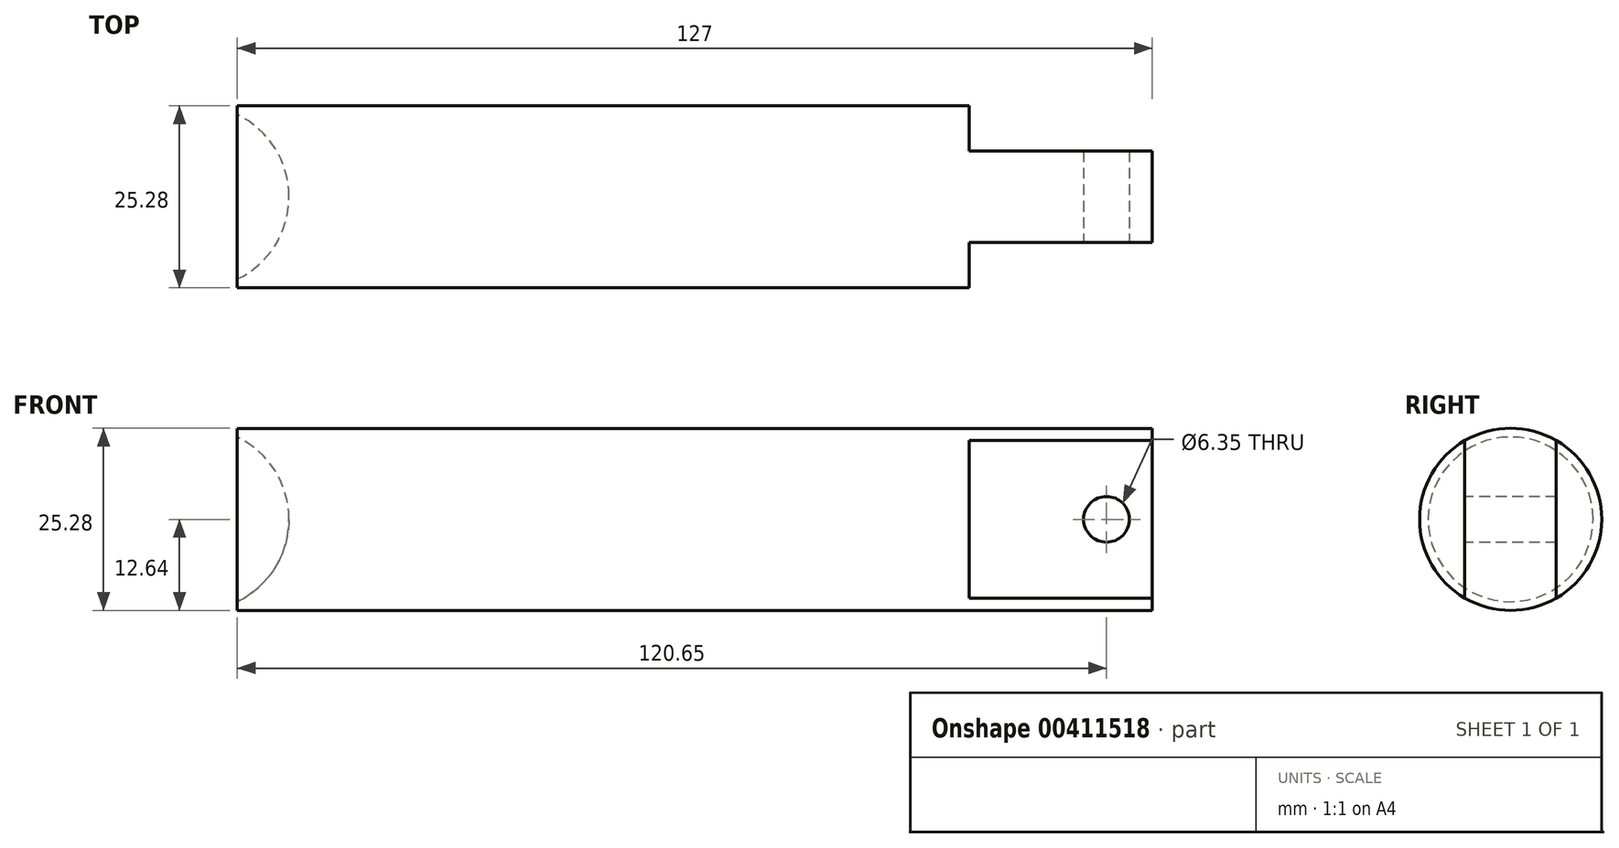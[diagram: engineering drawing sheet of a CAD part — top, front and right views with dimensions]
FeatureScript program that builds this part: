
annotation { "Feature Type Name" : "Feature", "Feature Type Description" : "" }
export const myFeature = defineFeature(function(context is Context, id is Id, definition is map)
    precondition{}
    {
        {
            var Q0;
            Q0=qCreatedBy(makeId("Right.planeOp"),FACE);
            var sketch = newSketch(context, id + "F0", { "sketchPlane" : qUnion([Q0])});
            skCircle(sketch, "E0", {"center": v(0, 0) * mm, "radius": 12.64 * mm});
            skSolve(sketch);
        }
        {
            var Q0;
            Q0 = qSketchRegion(id + "F0", true);
            extrude(context, id + "F1", {"entities" : qUnion([Q0]), "depth" : 127 * mm});
        }
        {
            var Q0;
            Q0=makeQuery(id+"F1.opExtrude","CAP_FACE",FACE,{"disambiguationData":[OSD([sQuery(id+"F0.wireOp",EDGE,"E0")])],"isStart":false});
            var sketch = newSketch(context, id + "F2", { "sketchPlane" : qUnion([Q0])});
            skArc(sketch, "E1.0", {"start": v(6.35, -10.93) * mm, "mid": v(12.64, 0) * mm, "end": v(6.35, 10.93) * mm});
            skLineSegment(sketch, "E2", {"start": v(-6.35, 10.93) * mm, "end": v(-6.35, -10.93) * mm});
            skLineSegment(sketch, "E3", {"start": v(6.35, 10.93) * mm, "end": v(6.35, -10.93) * mm});
            skArc(sketch, "E4.trimOffspring", {"start": v(-6.35, 10.93) * mm, "mid": v(-12.64, 0) * mm, "end": v(-6.35, -10.93) * mm});
            skSolve(sketch);
        }
        {
            var Q0;
            Q0=makeQuery(id+"F2.imprint","IMPRINT",FACE,{"disambiguationData":[TD([[makeQuery(id+"F2.imprint","IMPRINT",EDGE,{"derivedFrom":sQuery(id+"F2.wireOp",EDGE,"E2")}),-1.0]])]});
            var Q1;
            Q1=makeQuery(id+"F2.imprint","IMPRINT",FACE,{"disambiguationData":[TD([[makeQuery(id+"F2.imprint","IMPRINT",EDGE,{"derivedFrom":sQuery(id+"F2.wireOp",EDGE,"E1.0")}),1.0]])]});
            extrude(context, id + "F3", {"entities" : qUnion([Q0, Q1]), "operationType" : NewBodyOperationType.REMOVE, "oppositeDirection" : true, "depth" : 25.4 * mm});
        }
        {
            var Q0;
            Q0=makeQuery(id+"F3.boolean.opBoolean","COPY",FACE,{"derivedFrom":makeQuery(id+"F3.opExtrude","SWEPT_FACE",FACE,{"disambiguationData":[OSD([sQuery(id+"F2.wireOp",EDGE,"E2")])]})});
            var sketch = newSketch(context, id + "F4", { "sketchPlane" : qUnion([Q0])});
            skCircle(sketch, "E5", {"center": v(120.65, 0) * mm, "radius": 3.18 * mm});
            skPoint(sketch, "E5.centerSnap0", {"position": v(127, 0) * mm});
            skSolve(sketch);
        }
        {
            var Q0;
            Q0 = qSketchRegion(id + "F4", true);
            extrude(context, id + "F5", {"entities" : qUnion([Q0]), "operationType" : NewBodyOperationType.REMOVE, "oppositeDirection" : true, "depth" : 25.4 * mm});
        }
        {
            var Q0;
            Q0=qCreatedBy(makeId("Front.planeOp"),FACE);
            var sketch = newSketch(context, id + "F6", { "sketchPlane" : qUnion([Q0])});
            skArc(sketch, "E6", {"start": v(7.18, 0) * mm, "mid": v(4.48, 7.82) * mm, "end": v(-2.46, 12.33) * mm});
            skLineSegment(sketch, "E7", {"start": v(-2.46, 0) * mm, "end": v(7.18, 0) * mm});
            skPoint(sketch, "E7.endSnap0", {"position": v(7.18, 0) * mm});
            skLineSegment(sketch, "E8", {"start": v(-2.46, 12.33) * mm, "end": v(-2.46, 0) * mm});
            skPoint(sketch, "E9.orphan", {"position": v(-4.45, 0) * mm});
            skSolve(sketch);
        }
        {
            var Q0;
            Q0 = qSketchRegion(id + "F6", true);
            var Q1;
            Q1=sQuery(id+"F6.wireOp",EDGE,"E7");
            revolve(context, id + "F7", {"operationType" : NewBodyOperationType.REMOVE, "entities" : qUnion([Q0]), "axis" : qUnion([Q1]), "revolveType" : RevolveType.FULL});
        }
    });
